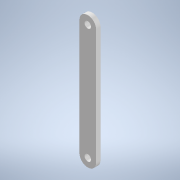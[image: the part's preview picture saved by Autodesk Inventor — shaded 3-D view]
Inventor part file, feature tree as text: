
AUTODESK INVENTOR PART (.ipt)
format: ipt  version: 2022 (Build 260153000, 153)  size: 105,984 bytes
history: native  units: mm
features: other x2, extrude x1, sketch x1, reference x1
ambient origin geometry x8: Origin, YZ Plane, XZ Plane, XY Plane, X Axis, Y Axis, Z Axis, Center Point
bodies: Solid1 (feature_tree)
feature tree (5):
  extrude  "Extrusion1"  Depth=3.2mm
  sketch  "Sketch1"  dims[d0=12.0mm d1=82.5mm d3=3.2mm d4=0.0mm]
  reference  "Reference1"
  other  "Caja_Reductora.iam"
  other  "Acople_TransPot:1"
